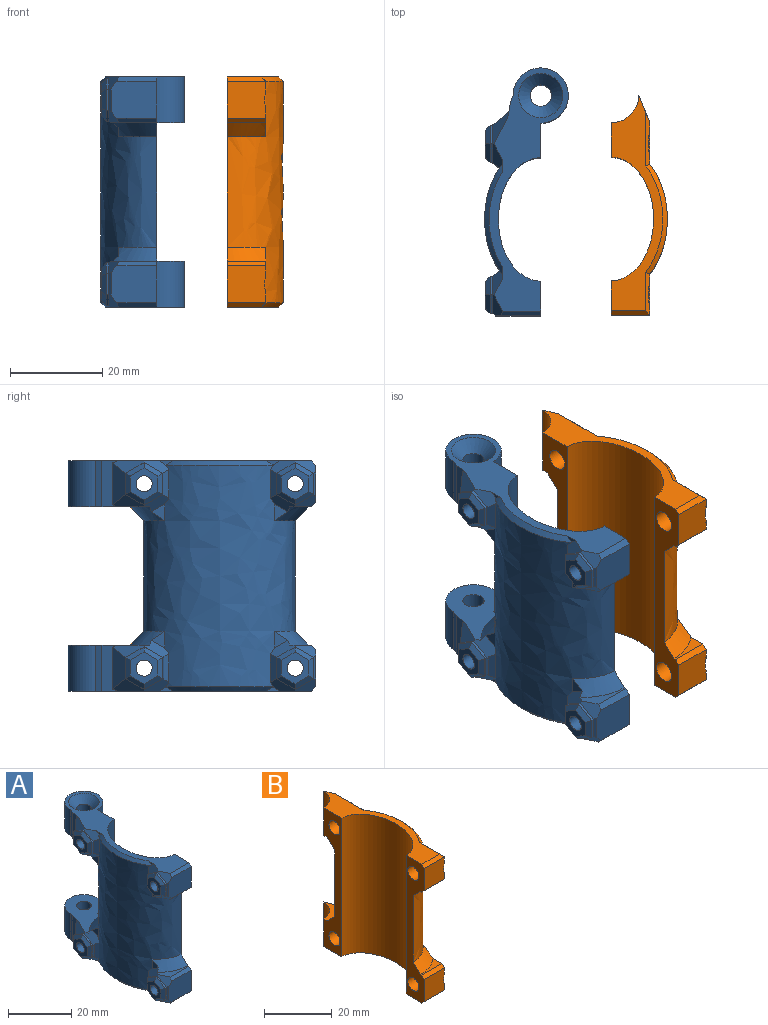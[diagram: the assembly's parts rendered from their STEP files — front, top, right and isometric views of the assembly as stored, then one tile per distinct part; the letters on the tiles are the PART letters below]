
ASSEMBLY  parts=2 mates=1
PART A: 125 faces, bbox 18.4x54x50.2 mm
  f0: plane 2.94x0.88mm, normal (-1,0,0), area 1.2mm2, adj f25,f82,f91
  f1: plane 2.94x0.88mm, normal (-1,0,0), area 1.2mm2, adj f25,f71,f91
  f2: plane 0.38x0.22mm, normal (-1,0,0), area 0mm2, adj f25,f69,f89
  f3: plane 0.38x0.22mm, normal (-1,0,0), area 0mm2, adj f28,f70,f88
  f4: plane 3.87x3.13mm, normal (-1,0,0), area 5.5mm2, adj f17,f77,f94
  f5: plane 0.38x0.22mm, normal (-1,0,0), area 0mm2, adj f24,f64,f86
  f6: plane 2.94x0.88mm, normal (-1,0,0), area 1.2mm2, adj f24,f66,f90
  f7: plane 0.38x0.22mm, normal (-1,0,0), area 0mm2, adj f29,f63,f87
  f8: plane 3.87x3.13mm, normal (-1,0,0), area 5.5mm2, adj f17,f80,f95
  f9: plane 3.87x3.13mm, normal (-1,0,0), area 5.5mm2, adj f17,f72,f92
  f10: plane 9.9x8mm, normal (0,-1,0), area 77.5mm2, adj f20,f68,f69,f70,f88,f89
  f11: cylinder r=6mm len=12mm, axis (0,0,-1), area 282.7mm2, adj f12,f22,f25,f27
  f12: plane 10x1.36mm, normal (-0.93,0.37,0), area 14.6mm2, adj f11,f25,f27,f97
  f13: cylinder r=2.3mm len=7.5mm, axis (0,0,-1), area 108.4mm2, adj f27,f84
  f14: cylinder r=6mm len=12mm, axis (0,0,-1), area 282.7mm2, adj f15,f22,f24,f26
  f15: plane 10x1.36mm, normal (-0.93,0.37,0), area 14.6mm2, adj f14,f24,f26,f96
  f16: plane 2.94x0.88mm, normal (-1,0,0), area 1.2mm2, adj f24,f75,f90
  f17: extruded ~48x32.8mm, area 1662.9mm2, adj f4,f8,f9,f18,f20,f22,f65,f66
  f18: plane 3.87x3.13mm, normal (-1,0,0), area 5.5mm2, adj f17,f65,f93
  f19: plane 9.9x8mm, normal (0,-1,0), area 77.5mm2, adj f20,f62,f63,f64,f86,f87
  f20: plane 50x7.5mm, normal (1,0,0), area 227.8mm2, adj f10,f17,f19,f21,f24,f25,f28,f29
  f21: extruded ~50x26.8mm, area 1790.4mm2, adj f20,f22,f24,f25
  f22: plane 50x7.5mm, normal (1,0,0), area 229.8mm2, adj f11,f14,f17,f21,f24,f25,f26,f27
  f23: cylinder r=2.3mm len=7.5mm, axis (0,0,-1), area 108.4mm2, adj f26,f85
  f24: plane 52.93x17.33mm, normal (0,0,1), area 252.4mm2, adj f5,f6,f14,f15,f16,f20,f21,f22
  f25: plane 52.93x17.33mm, normal (0,0,-1), area 252.4mm2, adj f0,f1,f2,f11,f12,f20,f21,f22
  f26: plane 17.8x16.18mm, normal (0,0,-1), area 134.1mm2, adj f14,f15,f22,f23,f77,f78,f94,f96
  f27: plane 17.8x16.18mm, normal (0,0,1), area 134.1mm2, adj f11,f12,f13,f22,f79,f80,f95,f97
  f28: plane 10.17x4.79mm, normal (0,0,1), area 16.7mm2, adj f3,f20,f70,f72,f88,f92
  f29: plane 10.17x4.79mm, normal (0,0,-1), area 16.7mm2, adj f7,f20,f63,f65,f87,f93
  f30: cylinder r=1.75mm len=12mm, axis (1,0,0), area 131.9mm2, adj f22,f40
  f31: cylinder r=1.75mm len=12mm, axis (1,0,0), area 131.9mm2, adj f22,f47
  f32: cylinder r=1.75mm len=12mm, axis (1,0,0), area 131.9mm2, adj f20,f54
  f33: cylinder r=1.75mm len=12mm, axis (1,0,0), area 131.9mm2, adj f20,f61
  f34: plane 4x2.31mm, normal (0,-0.5,0.87), area 2.8mm2, adj f35,f39,f75,f122
  f35: plane 4.62x0.61mm, normal (0,-1,0), area 2.8mm2, adj f34,f36,f76,f120
  f36: plane 4x2.31mm, normal (0,-0.5,-0.87), area 2.8mm2, adj f35,f37,f77,f118
  f37: plane 4.11x2.37mm, normal (0,0.5,-0.87), area 2.8mm2, adj f36,f38,f78,f98,f119
  f38: plane 4.62x0.47mm, normal (0,1,0), area 2.2mm2, adj f37,f39,f98,f121
  f39: plane 4.11x2.37mm, normal (0,0.5,0.87), area 2.8mm2, adj f34,f38,f74,f98,f123
  f40: plane 6.93x6mm, normal (-1,0,0), area 21.6mm2, adj f30,f118,f119,f120,f121,f122,f123
  f41: plane 4.17x2.41mm, normal (0,-0.5,0.87), area 2.8mm2, adj f42,f46,f80,f103,f124
  f42: plane 4.62x0.19mm, normal (0,-1,0), area 0.9mm2, adj f41,f43,f105,f124
  f43: plane 4.17x2.41mm, normal (0,-0.5,-0.87), area 2.8mm2, adj f42,f44,f82,f104,f124
  f44: plane 4.11x2.37mm, normal (0,0.5,-0.87), area 2.8mm2, adj f43,f45,f83,f99,f102
  f45: plane 4.62x0.47mm, normal (0,1,0), area 2.2mm2, adj f44,f46,f99,f100
  f46: plane 4.11x2.37mm, normal (0,0.5,0.87), area 2.8mm2, adj f41,f45,f79,f99,f101
  f47: plane 6.93x6mm, normal (-1,0,0), area 21.6mm2, adj f31,f100,f101,f102,f103,f104,f105
  f48: plane 4x2.31mm, normal (0,-0.5,0.87), area 2.8mm2, adj f49,f53,f70,f116
  f49: plane 4.62x0.61mm, normal (0,-1,0), area 2.8mm2, adj f48,f50,f68,f114
  f50: plane 4x2.31mm, normal (0,-0.5,-0.87), area 2.8mm2, adj f49,f51,f69,f112
  f51: plane 4x2.31mm, normal (0,0.5,-0.87), area 2.8mm2, adj f50,f52,f71,f113
  f52: plane 4.62x0.61mm, normal (0,1,0), area 2.8mm2, adj f51,f53,f73,f115
  f53: plane 4x2.31mm, normal (0,0.5,0.87), area 2.8mm2, adj f48,f52,f72,f117
  f54: plane 6.93x6mm, normal (-1,0,0), area 21.6mm2, adj f32,f112,f113,f114,f115,f116,f117
  f55: plane 4x2.31mm, normal (0,-0.5,0.87), area 2.8mm2, adj f56,f60,f64,f107
  f56: plane 4.62x0.61mm, normal (0,-1,0), area 2.8mm2, adj f55,f57,f62,f109
  f57: plane 4x2.31mm, normal (0,-0.5,-0.87), area 2.8mm2, adj f56,f58,f63,f111
  f58: plane 4x2.31mm, normal (0,0.5,-0.87), area 2.8mm2, adj f57,f59,f65,f110
  f59: plane 4.62x0.61mm, normal (0,1,0), area 2.8mm2, adj f58,f60,f67,f108
  f60: plane 4x2.31mm, normal (0,0.5,0.87), area 2.8mm2, adj f55,f59,f66,f106
  f61: plane 6.93x6mm, normal (-1,0,0), area 21.6mm2, adj f33,f106,f107,f108,f109,f110,f111
  f62: plane 5.2x0.5mm, normal (-0.71,-0.71,0), area 3.5mm2, adj f19,f56,f63,f64
  f63: plane 4.5x2.69mm, normal (-0.71,-0.35,-0.61), area 9.8mm2, adj f7,f19,f29,f57,f62,f65,f87
  f64: plane 4.5x2.69mm, normal (-0.71,-0.35,0.61), area 9.8mm2, adj f5,f19,f24,f55,f62,f66,f86
  f65: plane 5.39x3.73mm, normal (-0.71,0.35,-0.61), area 12.5mm2, adj f17,f18,f29,f58,f63,f67,f93
  f66: plane 5.37x2.69mm, normal (-0.71,0.35,0.61), area 11mm2, adj f6,f17,f24,f60,f64,f67,f90
  f67: plane 6.2x1.37mm, normal (-0.71,0.71,0), area 10.5mm2, adj f17,f59,f65,f66
  f68: plane 5.2x0.5mm, normal (-0.71,-0.71,0), area 3.5mm2, adj f10,f49,f69,f70
  f69: plane 4.5x2.69mm, normal (-0.71,-0.35,-0.61), area 9.8mm2, adj f2,f10,f25,f50,f68,f71,f89
  f70: plane 4.5x2.69mm, normal (-0.71,-0.35,0.61), area 9.8mm2, adj f3,f10,f28,f48,f68,f72,f88
  f71: plane 5.37x2.69mm, normal (-0.71,0.35,-0.61), area 11mm2, adj f1,f17,f25,f51,f69,f73,f91
  f72: plane 5.39x3.73mm, normal (-0.71,0.35,0.61), area 12.5mm2, adj f9,f17,f28,f53,f70,f73,f92
  f73: plane 6.2x1.37mm, normal (-0.71,0.71,0), area 10.5mm2, adj f17,f52,f71,f72
  f74: plane 6.95x3.43mm, normal (-0.71,0.35,0.61), area 15.1mm2, adj f24,f39,f75,f96,f98
  f75: plane 5.37x2.69mm, normal (-0.71,-0.35,0.61), area 11mm2, adj f16,f17,f24,f34,f74,f76,f90
  f76: plane 6.2x1.37mm, normal (-0.71,-0.71,0), area 10.5mm2, adj f17,f35,f75,f77
  f77: plane 5.39x3.73mm, normal (-0.71,-0.35,-0.61), area 12.5mm2, adj f4,f17,f26,f36,f76,f78,f94
  f78: plane 6.95x3.43mm, normal (-0.71,0.35,-0.61), area 15.1mm2, adj f26,f37,f77,f96,f98
  f79: plane 6.95x3.43mm, normal (-0.71,0.35,0.61), area 15.1mm2, adj f27,f46,f80,f97,f99
  f80: plane 5.39x3.83mm, normal (-0.71,-0.35,0.61), area 12.6mm2, adj f8,f17,f27,f41,f79,f81,f95,f124
  f81: plane 6.2x1.08mm, normal (-0.71,-0.71,0), area 8.5mm2, adj f17,f80,f82,f124
  f82: plane 5.37x2.79mm, normal (-0.71,-0.35,-0.61), area 11.1mm2, adj f0,f17,f25,f43,f81,f83,f91,f124
  f83: plane 6.95x3.43mm, normal (-0.71,0.35,-0.61), area 15.1mm2, adj f25,f44,f82,f97,f99
  f84: cone r=4.8mm half-angle=45deg, axis (0,0,-1), area 78.9mm2, adj f13,f25
  f85: cone r=2.3mm half-angle=45deg, axis (0,0,1), area 78.9mm2, adj f23,f24
  f86: plane 8.68x1mm, normal (0,-0.71,0.71), area 12mm2, adj f5,f19,f20,f24,f64
  f87: plane 8.68x1mm, normal (0,-0.71,-0.71), area 12mm2, adj f7,f19,f20,f29,f63
  f88: plane 8.68x1mm, normal (0,-0.71,0.71), area 12mm2, adj f3,f10,f20,f28,f70
  f89: plane 8.68x1mm, normal (0,-0.71,-0.71), area 12mm2, adj f2,f10,f20,f25,f69
  f90: bspline ~25.77x5.38mm, area 33mm2, adj f6,f16,f17,f24,f66,f75
  f91: bspline ~25.77x5.38mm, area 33mm2, adj f0,f1,f17,f25,f71,f82
  f92: bspline ~11.76x7.96mm, area 41.4mm2, adj f9,f17,f20,f28,f72
  f93: bspline ~11.76x7.96mm, area 41.4mm2, adj f17,f18,f20,f29,f65
  f94: bspline ~10.76x7.5mm, area 41.4mm2, adj f4,f17,f22,f26,f77
  f95: bspline ~10.76x7.5mm, area 41.4mm2, adj f8,f17,f22,f27,f80
  f96: plane 10x3.41mm, normal (-0.98,0.19,0), area 22.9mm2, adj f15,f24,f26,f74,f78,f98
  f97: plane 10x3.41mm, normal (-0.98,0.19,0), area 22.9mm2, adj f12,f25,f27,f79,f83,f99
  f98: plane 9.14x3.57mm, normal (-0.64,0.77,0), area 31.1mm2, adj f37,f38,f39,f74,f78,f96
  f99: plane 9.14x3.57mm, normal (-0.64,0.77,0), area 31.1mm2, adj f44,f45,f46,f79,f83,f97
  f100: plane 4.62x1mm, normal (-0.71,0.71,0), area 5.7mm2, adj f45,f47,f101,f102
  f101: plane 4x2.89mm, normal (-0.71,0.35,0.61), area 5.7mm2, adj f46,f47,f100,f103
  f102: plane 4x2.89mm, normal (-0.71,0.35,-0.61), area 5.7mm2, adj f44,f47,f100,f104
  f103: plane 4x2.89mm, normal (-0.71,-0.35,0.61), area 5.7mm2, adj f41,f47,f101,f105
  f104: plane 4x2.89mm, normal (-0.71,-0.35,-0.61), area 5.7mm2, adj f43,f47,f102,f105
  f105: plane 4.62x1mm, normal (-0.71,-0.71,0), area 5.7mm2, adj f42,f47,f103,f104
  f106: plane 4x2.89mm, normal (-0.71,0.35,0.61), area 5.7mm2, adj f60,f61,f107,f108
  f107: plane 4x2.89mm, normal (-0.71,-0.35,0.61), area 5.7mm2, adj f55,f61,f106,f109
  f108: plane 4.62x1mm, normal (-0.71,0.71,0), area 5.7mm2, adj f59,f61,f106,f110
  f109: plane 4.62x1mm, normal (-0.71,-0.71,0), area 5.7mm2, adj f56,f61,f107,f111
  f110: plane 4x2.89mm, normal (-0.71,0.35,-0.61), area 5.7mm2, adj f58,f61,f108,f111
  f111: plane 4x2.89mm, normal (-0.71,-0.35,-0.61), area 5.7mm2, adj f57,f61,f109,f110
  f112: plane 4x2.89mm, normal (-0.71,-0.35,-0.61), area 5.7mm2, adj f50,f54,f113,f114
  f113: plane 4x2.89mm, normal (-0.71,0.35,-0.61), area 5.7mm2, adj f51,f54,f112,f115
  f114: plane 4.62x1mm, normal (-0.71,-0.71,0), area 5.7mm2, adj f49,f54,f112,f116
  f115: plane 4.62x1mm, normal (-0.71,0.71,0), area 5.7mm2, adj f52,f54,f113,f117
  f116: plane 4x2.89mm, normal (-0.71,-0.35,0.61), area 5.7mm2, adj f48,f54,f114,f117
  f117: plane 4x2.89mm, normal (-0.71,0.35,0.61), area 5.7mm2, adj f53,f54,f115,f116
  f118: plane 4x2.89mm, normal (-0.71,-0.35,-0.61), area 5.7mm2, adj f36,f40,f119,f120
  f119: plane 4x2.89mm, normal (-0.71,0.35,-0.61), area 5.7mm2, adj f37,f40,f118,f121
  f120: plane 4.62x1mm, normal (-0.71,-0.71,0), area 5.7mm2, adj f35,f40,f118,f122
  f121: plane 4.62x1mm, normal (-0.71,0.71,0), area 5.7mm2, adj f38,f40,f119,f123
  f122: plane 4x2.89mm, normal (-0.71,-0.35,0.61), area 5.7mm2, adj f34,f40,f120,f123
  f123: plane 4x2.89mm, normal (-0.71,0.35,0.61), area 5.7mm2, adj f39,f40,f121,f122
  f124: plane 4.96x0.71mm, normal (-0.38,-0.92,0), area 3.5mm2, adj f41,f42,f43,f80,f81,f82
PART B: 50 faces, bbox 14x49.2x51.1 mm
  f0: plane 2.33x1.85mm, normal (1,0,0), area 1.7mm2, adj f10,f32,f37
  f1: plane 2.33x1.85mm, normal (1,0,0), area 1.7mm2, adj f21,f33,f41
  f2: plane 2.33x1.85mm, normal (1,0,0), area 1.7mm2, adj f14,f35,f43
  f3: plane 2.33x1.85mm, normal (1,0,0), area 1.7mm2, adj f21,f34,f39
  f4: plane 9.42x6.75mm, normal (1,0,0), area 16.2mm2, adj f14,f21,f27,f35,f49
  f5: plane 2.33x1.85mm, normal (1,0,0), area 1.7mm2, adj f9,f34,f39
  f6: plane 9.42x6.75mm, normal (1,0,0), area 15.7mm2, adj f19,f21,f25,f33,f45,f46
  f7: plane 2.33x1.85mm, normal (1,0,0), area 1.7mm2, adj f21,f32,f37
  f8: plane 9.42x6.75mm, normal (1,0,0), area 16.2mm2, adj f9,f21,f26,f34,f48
  f9: plane 10.24x6.24mm, normal (0.93,0.37,0), area 62.7mm2, adj f5,f8,f12,f23,f26,f34,f39
  f10: plane 9.24x8.85mm, normal (0,-1,0), area 66.5mm2, adj f0,f11,f18,f32,f36,f44
  f11: plane 9.42x6.75mm, normal (1,0,0), area 15.7mm2, adj f10,f21,f24,f32,f44,f47
  f12: cylinder r=6mm len=10mm, axis (0,0,-1), area 94.2mm2, adj f9,f16,f23,f26
  f13: plane 2.33x1.85mm, normal (1,0,0), area 1.7mm2, adj f21,f35,f43
  f14: plane 10.24x6.24mm, normal (0.93,0.37,0), area 62.7mm2, adj f2,f4,f15,f22,f27,f35,f43
  f15: cylinder r=6mm len=10mm, axis (0,0,-1), area 94.2mm2, adj f14,f16,f22,f27
  f16: plane 50x7.5mm, normal (-1,0,0), area 215.8mm2, adj f12,f15,f17,f21,f22,f23,f26,f27
  f17: extruded ~50x26.8mm, area 1790.4mm2, adj f16,f18,f22,f23
  f18: plane 50x7.5mm, normal (-1,0,0), area 213.8mm2, adj f10,f17,f19,f21,f22,f23,f24,f25
  f19: plane 9.24x8.85mm, normal (0,-1,0), area 66.5mm2, adj f6,f18,f20,f33,f40,f45
  f20: plane 2.33x1.85mm, normal (1,0,0), area 1.7mm2, adj f19,f33,f41
  f21: extruded ~48x32.8mm, area 1730.6mm2, adj f1,f3,f4,f6,f7,f8,f11,f13
  f22: plane 46.98x11.38mm, normal (0,0,1), area 182.7mm2, adj f14,f15,f16,f17,f18,f40,f41,f42
  f23: plane 46.98x11.38mm, normal (0,0,-1), area 182.7mm2, adj f9,f12,f16,f17,f18,f36,f37,f38
  f24: plane 8.48x3.78mm, normal (0,0,1), area 12.8mm2, adj f11,f18,f44,f47
  f25: plane 8.48x3.78mm, normal (0,0,-1), area 12.8mm2, adj f6,f18,f45,f46
  f26: plane 10.78x8.48mm, normal (0,0,1), area 36.1mm2, adj f8,f9,f12,f16,f48
  f27: plane 10.78x8.48mm, normal (0,0,-1), area 36.1mm2, adj f4,f14,f15,f16,f49
  f28: cylinder r=2.3mm len=5.9mm, axis (-1,0,0), area 85.2mm2, adj f18,f21,f33
  f29: cylinder r=2.3mm len=5.9mm, axis (-1,0,0), area 85.2mm2, adj f18,f21,f32
  f30: cylinder r=2.3mm len=5.9mm, axis (-1,0,0), area 85.2mm2, adj f16,f21,f34
  f31: cylinder r=2.3mm len=5.9mm, axis (-1,0,0), area 85.2mm2, adj f16,f21,f35
  f32: cone r=4.8mm half-angle=45deg, axis (1,0,0), area 67.1mm2, adj f0,f7,f10,f11,f21,f29,f37
  f33: cone r=4.8mm half-angle=45deg, axis (1,0,0), area 67.1mm2, adj f1,f6,f19,f20,f21,f28,f41
  f34: cone r=4.8mm half-angle=45deg, axis (1,0,0), area 67.1mm2, adj f3,f5,f8,f9,f21,f30,f39
  f35: cone r=4.8mm half-angle=45deg, axis (1,0,0), area 67.1mm2, adj f2,f4,f13,f14,f21,f31,f43
  f36: plane 8.4x1mm, normal (0,-0.71,-0.71), area 11.2mm2, adj f10,f18,f23,f37
  f37: plane 10.48x2.13mm, normal (0.71,0,-0.71), area 10.3mm2, adj f0,f7,f23,f32,f36,f38
  f38: bspline ~24.37x4.8mm, area 35.5mm2, adj f21,f23,f37,f39
  f39: plane 12.99x2.13mm, normal (0.71,0,-0.71), area 12.7mm2, adj f3,f5,f9,f23,f34,f38
  f40: plane 8.4x1mm, normal (0,-0.71,0.71), area 11.2mm2, adj f18,f19,f22,f41
  f41: plane 10.48x2.13mm, normal (0.71,0,0.71), area 10.3mm2, adj f1,f20,f22,f33,f40,f42
  f42: bspline ~24.37x4.8mm, area 35.5mm2, adj f21,f22,f41,f43
  f43: plane 12.99x2.13mm, normal (0.71,0,0.71), area 12.7mm2, adj f2,f13,f14,f22,f35,f42
  f44: plane 8.4x1mm, normal (0,-0.71,0.71), area 11.9mm2, adj f10,f11,f18,f24
  f45: plane 8.4x1mm, normal (0,-0.71,-0.71), area 11.9mm2, adj f6,f18,f19,f25
  f46: bspline ~11.76x7.96mm, area 40.8mm2, adj f6,f18,f21,f25
  f47: bspline ~11.76x7.96mm, area 40.8mm2, adj f11,f18,f21,f24
  f48: bspline ~11.76x7.96mm, area 40.8mm2, adj f8,f16,f21,f26
  f49: bspline ~11.76x7.96mm, area 40.8mm2, adj f4,f16,f21,f27
PLACE A t=(-6.74,0.11,7.09)mm
PLACE B t=(8.57,0.2,7.09)mm
MATE planar B.f23 <-> A.f25  axis (0,0,-1) through (13.93,2.72,-17.91)mm
